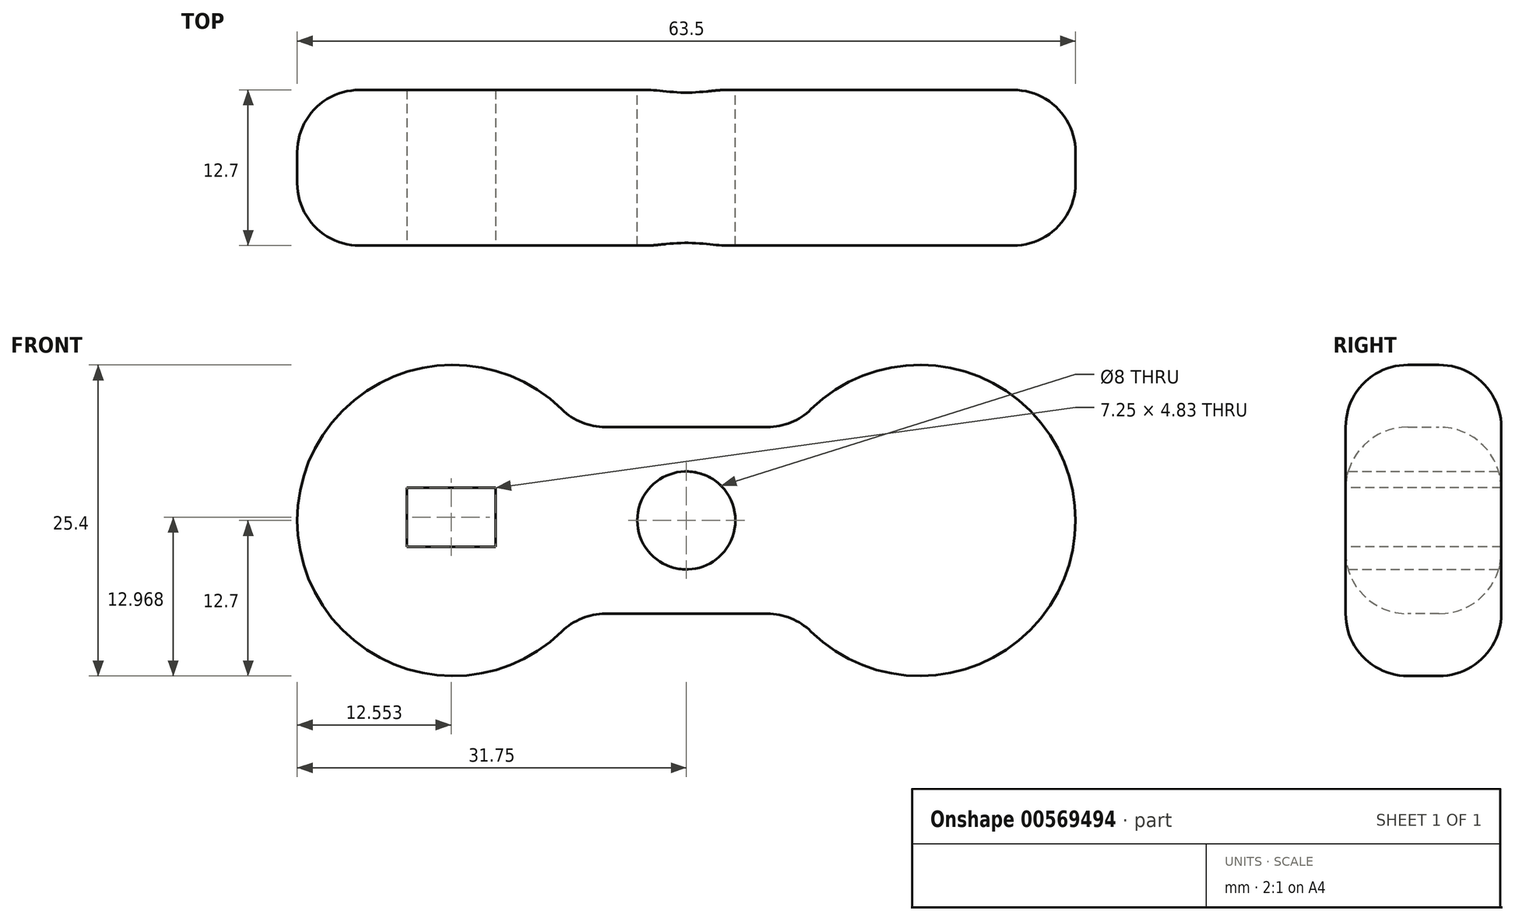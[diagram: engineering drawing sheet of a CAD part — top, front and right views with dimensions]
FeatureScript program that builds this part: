
annotation { "Feature Type Name" : "Feature", "Feature Type Description" : "" }
export const myFeature = defineFeature(function(context is Context, id is Id, definition is map)
    precondition{}
    {
        {
            var Q0;
            Q0=qCreatedBy(makeId("Front.planeOp"),FACE);
            var sketch = newSketch(context, id + "F0", { "sketchPlane" : qUnion([Q0])});
            skLineSegment(sketch, "E0.bottom", {"start": v(-19.05, 7.62) * mm, "end": v(19.05, 7.62) * mm});
            skLineSegment(sketch, "E0.top", {"start": v(-19.05, -7.62) * mm, "end": v(19.05, -7.62) * mm});
            skLineSegment(sketch, "E0.left", {"start": v(-19.05, 7.62) * mm, "end": v(-19.05, -7.62) * mm});
            skLineSegment(sketch, "E0.right", {"start": v(19.05, 7.62) * mm, "end": v(19.05, -7.62) * mm});
            skPoint(sketch, "E0.middle", {"position": v(0, 0) * mm});
            skCircle(sketch, "E1", {"center": v(-19.05, 0) * mm, "radius": 12.7 * mm});
            skCircle(sketch, "E2", {"center": v(19.05, 0) * mm, "radius": 12.7 * mm});
            skCircle(sketch, "E3", {"center": v(0, 0) * mm, "radius": 4 * mm});
            skSolve(sketch);
        }
        {
            var Q0;
            {var subQ0=sQuery(id+"F0.wireOp",EDGE,"E0.left");Q0=makeQuery(id+"F0.imprint","IMPRINT",FACE,{"disambiguationData":[TD([[makeQuery(id+"F0.imprint","IMPRINT",EDGE,{"derivedFrom":subQ0}),-1.0]])]});}
            var Q1;
            {var subQ0=sQuery(id+"F0.wireOp",EDGE,"E0.left");Q1=makeQuery(id+"F0.imprint","IMPRINT",FACE,{"disambiguationData":[TD([[makeQuery(id+"F0.imprint","IMPRINT",EDGE,{"derivedFrom":subQ0}),1.0]])]});}
            var Q2;
            Q2=makeQuery(id+"F0.imprint","IMPRINT",FACE,{"disambiguationData":[TD([[makeQuery(id+"F0.imprint","IMPRINT",EDGE,{"derivedFrom":sQuery(id+"F0.wireOp",EDGE,"E3")}),-1.0]])]});
            var Q3;
            {var subQ0=sQuery(id+"F0.wireOp",EDGE,"E0.right");Q3=makeQuery(id+"F0.imprint","IMPRINT",FACE,{"disambiguationData":[TD([[makeQuery(id+"F0.imprint","IMPRINT",EDGE,{"derivedFrom":subQ0}),-1.0]])]});}
            var Q4;
            {var subQ0=sQuery(id+"F0.wireOp",EDGE,"E0.right");Q4=makeQuery(id+"F0.imprint","IMPRINT",FACE,{"disambiguationData":[TD([[makeQuery(id+"F0.imprint","IMPRINT",EDGE,{"derivedFrom":subQ0}),1.0]])]});}
            extrude(context, id + "F1", {"entities" : qUnion([Q0, Q1, Q2, Q3, Q4]), "depth" : 12.7 * mm});
        }
        {
            var Q0;
            Q0=makeQuery(id+"F1.opExtrude","CAP_EDGE",EDGE,{"disambiguationData":[OSD([sQuery(id+"F0.wireOp",EDGE,"E1")])],"isStart":false});
            var Q1;
            Q1=makeQuery(id+"F1.opExtrude","CAP_EDGE",EDGE,{"disambiguationData":[OSD([sQuery(id+"F0.wireOp",EDGE,"E0.bottom")])],"isStart":false});
            var Q2;
            Q2=makeQuery(id+"F1.opExtrude","CAP_EDGE",EDGE,{"disambiguationData":[OSD([sQuery(id+"F0.wireOp",EDGE,"E2")])],"isStart":false});
            var Q3;
            Q3=makeQuery(id+"F1.opExtrude","CAP_EDGE",EDGE,{"disambiguationData":[OSD([sQuery(id+"F0.wireOp",EDGE,"E0.top")])],"isStart":false});
            var Q4;
            Q4=makeQuery(id+"F1.opExtrude","CAP_EDGE",EDGE,{"disambiguationData":[OSD([sQuery(id+"F0.wireOp",EDGE,"E2")])],"isStart":true});
            var Q5;
            Q5=makeQuery(id+"F1.opExtrude","CAP_EDGE",EDGE,{"disambiguationData":[OSD([sQuery(id+"F0.wireOp",EDGE,"E0.bottom")])],"isStart":true});
            var Q6;
            Q6=makeQuery(id+"F1.opExtrude","CAP_EDGE",EDGE,{"disambiguationData":[OSD([sQuery(id+"F0.wireOp",EDGE,"E0.top")])],"isStart":true});
            var Q7;
            Q7=makeQuery(id+"F1.opExtrude","CAP_EDGE",EDGE,{"disambiguationData":[OSD([sQuery(id+"F0.wireOp",EDGE,"E1")])],"isStart":true});
            var Q8;
            Q8=makeQuery(id+"F1.opExtrude","SWEPT_EDGE",EDGE,{"disambiguationData":[OSD([sQuery(id+"F0.wireOp",EDGE,"E0.top"),sQuery(id+"F0.wireOp",EDGE,"E1")])]});
            var Q9;
            Q9=makeQuery(id+"F1.opExtrude","SWEPT_EDGE",EDGE,{"disambiguationData":[OSD([sQuery(id+"F0.wireOp",EDGE,"E0.top"),sQuery(id+"F0.wireOp",EDGE,"E2")])]});
            var Q10;
            Q10=makeQuery(id+"F1.opExtrude","SWEPT_EDGE",EDGE,{"disambiguationData":[OSD([sQuery(id+"F0.wireOp",EDGE,"E0.bottom"),sQuery(id+"F0.wireOp",EDGE,"E1")])]});
            var Q11;
            Q11=makeQuery(id+"F1.opExtrude","SWEPT_EDGE",EDGE,{"disambiguationData":[OSD([sQuery(id+"F0.wireOp",EDGE,"E0.bottom"),sQuery(id+"F0.wireOp",EDGE,"E2")])]});
            fillet(context, id + "F2", {"entities" : qUnion([Q0, Q1, Q2, Q3, Q4, Q5, Q6, Q7, Q8, Q9, Q10, Q11]), "radius" : 5.08 * mm, "tangentPropagation" : true, "allowEdgeOverflow" : false});
        }
        {
            var Q0;
            Q0=makeQuery(id+"F2.opFillet","SPLIT",FACE,{"disambiguationData":[OD(0.0)],"derivedFrom":makeQuery(id+"F1.opExtrude","CAP_FACE",FACE,{"disambiguationData":[OSD([sQuery(id+"F0.wireOp",EDGE,"E0.bottom"),sQuery(id+"F0.wireOp",EDGE,"E0.top"),sQuery(id+"F0.wireOp",EDGE,"E1"),sQuery(id+"F0.wireOp",EDGE,"E2"),sQuery(id+"F0.wireOp",EDGE,"E3")])],"isStart":false})});
            var sketch = newSketch(context, id + "F3", { "sketchPlane" : qUnion([Q0])});
            skLineSegment(sketch, "E4.bottom", {"start": v(-22.82, 2.68) * mm, "end": v(-15.57, 2.68) * mm});
            skLineSegment(sketch, "E4.top", {"start": v(-22.82, -2.15) * mm, "end": v(-15.57, -2.15) * mm});
            skLineSegment(sketch, "E4.left", {"start": v(-22.82, 2.68) * mm, "end": v(-22.82, -2.15) * mm});
            skLineSegment(sketch, "E4.right", {"start": v(-15.57, 2.68) * mm, "end": v(-15.57, -2.15) * mm});
            skSolve(sketch);
        }
        {
            var Q0;
            Q0=makeQuery(id+"F3.imprint","IMPRINT",FACE,{"disambiguationData":[TD([[makeQuery(id+"F3.imprint","IMPRINT",EDGE,{"derivedFrom":sQuery(id+"F3.wireOp",EDGE,"E4.bottom")}),-1.0]])]});
            extrude(context, id + "F4", {"entities" : qUnion([Q0]), "operationType" : NewBodyOperationType.REMOVE, "oppositeDirection" : true, "depth" : 25.4 * mm, "offsetDistance" : 25.4 * mm});
        }
    });
